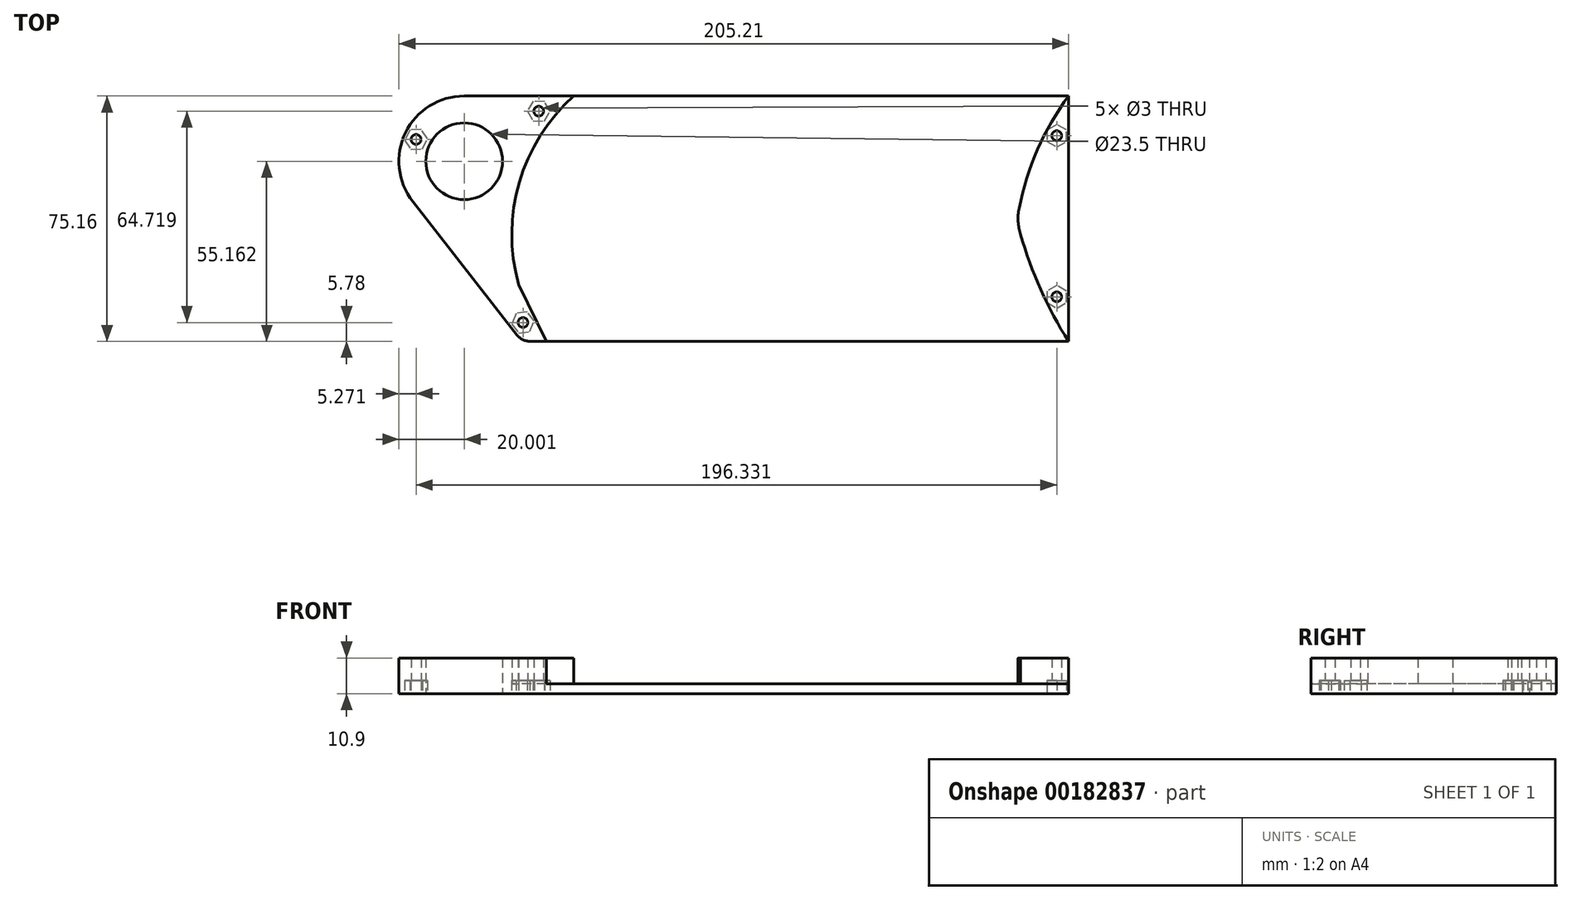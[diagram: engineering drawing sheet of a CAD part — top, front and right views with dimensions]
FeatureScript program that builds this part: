
annotation { "Feature Type Name" : "Feature", "Feature Type Description" : "" }
export const myFeature = defineFeature(function(context is Context, id is Id, definition is map)
    precondition{}
    {
        {
            var Q0;
            Q0=qCreatedBy(makeId("Top.planeOp"),FACE);
            var sketch = newSketch(context, id + "F0", { "sketchPlane" : qUnion([Q0])});
            skLineSegment(sketch, "E0", {"start": v(86, 37.87) * mm, "end": v(-99.2, 37.87) * mm});
            skLineSegment(sketch, "E1", {"start": v(86, -37.29) * mm, "end": v(-81.47, -37.29) * mm});
            skLineSegment(sketch, "E2.0", {"start": v(86, -37.29) * mm, "end": v(86, 37.87) * mm});
            skArc(sketch, "E3", {"start": v(70.84, 3.43) * mm, "mid": v(70.55, -0.57) * mm, "end": v(71.29, -4.5) * mm});
            skLineSegment(sketch, "E4", {"start": v(-73.97, -37.29) * mm, "end": v(-82.52, -19.87) * mm});
            skArc(sketch, "E5", {"start": v(-65.62, 37.87) * mm, "mid": v(-82.32, 11.42) * mm, "end": v(-82.52, -19.87) * mm});
            skArc(sketch, "E6", {"start": v(71.29, -4.5) * mm, "mid": v(77.46, -21.43) * mm, "end": v(86, -37.29) * mm});
            skCircle(sketch, "E7", {"center": v(-99.2, 17.87) * mm, "radius": 11.75 * mm});
            skLineSegment(sketch, "E8", {"start": v(-81.47, -37.29) * mm, "end": v(-114.97, 5.55) * mm});
            skArc(sketch, "E9", {"start": v(-99.2, 37.87) * mm, "mid": v(-117.19, 26.64) * mm, "end": v(-114.97, 5.55) * mm});
            skLineSegment(sketch, "E10", {"start": v(-73.97, -37.29) * mm, "end": v(-73.97, -48.25) * mm});
            skArc(sketch, "E11", {"start": v(86, 37.87) * mm, "mid": v(76.52, 21.49) * mm, "end": v(70.84, 3.43) * mm});
            skSolve(sketch);
        }
        {
            var Q0;
            Q0=makeQuery(id+"F0.imprint","IMPRINT",FACE,{"disambiguationData":[TD([[makeQuery(id+"F0.imprint","IMPRINT",EDGE,{"derivedFrom":sQuery(id+"F0.wireOp",EDGE,"E3")}),-1.0]])]});
            var sketch = newSketch(context, id + "F1", { "sketchPlane" : qUnion([Q0])});
            skSolve(sketch);
        }
        {
            var Q0;
            Q0 = qSketchRegion(id + "F1", true);
            var Q1;
            Q1=makeQuery(id+"F0.imprint","IMPRINT",FACE,{"disambiguationData":[TD([[makeQuery(id+"F0.imprint","IMPRINT",EDGE,{"derivedFrom":sQuery(id+"F0.wireOp",EDGE,"E3")}),-1.0]])]});
            extrude(context, id + "F2", {"entities" : qUnion([Q0, Q1]), "oppositeDirection" : true, "depth" : 3 * mm});
        }
        {
            var Q0;
            {var subQ3=sQuery(id+"F0.wireOp",EDGE,"E4");Q0=makeQuery(id+"F0.imprint","IMPRINT",FACE,{"disambiguationData":[TD([[makeQuery(id+"F0.imprint","IMPRINT",EDGE,{"derivedFrom":subQ3}),1.0]])]});}
            extrude(context, id + "F3", {"entities" : qUnion([Q0]), "depth" : 7.9 * mm});
        }
        {
            var Q0;
            {var subQ0=sQuery(id+"F0.wireOp",EDGE,"E2.0");Q0=makeQuery(id+"F0.imprint","IMPRINT",FACE,{"disambiguationData":[TD([[makeQuery(id+"F0.imprint","IMPRINT",EDGE,{"derivedFrom":subQ0}),1.0]])]});}
            extrude(context, id + "F4", {"entities" : qUnion([Q0]), "depth" : 7.9 * mm});
        }
        {
            var Q0;
            Q0=makeQuery(id+"F3.opExtrude","CAP_FACE",FACE,{"disambiguationData":[OSD([sQuery(id+"F0.wireOp",EDGE,"E0"),sQuery(id+"F0.wireOp",EDGE,"E1"),sQuery(id+"F0.wireOp",EDGE,"E4"),sQuery(id+"F0.wireOp",EDGE,"E5"),sQuery(id+"F0.wireOp",EDGE,"E7"),sQuery(id+"F0.wireOp",EDGE,"E8"),sQuery(id+"F0.wireOp",EDGE,"E9")])],"isStart":true});
            var Q1;
            Q1=makeQuery(id+"F4.opExtrude","CAP_FACE",FACE,{"disambiguationData":[OSD([sQuery(id+"F0.wireOp",EDGE,"E0"),sQuery(id+"F0.wireOp",EDGE,"E1"),sQuery(id+"F0.wireOp",EDGE,"E2.0"),sQuery(id+"F0.wireOp",EDGE,"E3"),sQuery(id+"F0.wireOp",EDGE,"uJdoGhJC-Amh7-iMku-Pf1O-IdhWUITwSaAr"),sQuery(id+"F0.wireOp",EDGE,"E6")])],"isStart":true});
            extrude(context, id + "F5", {"entities" : qUnion([Q0, Q1]), "depth" : 3 * mm});
        }
        {
            var Q0;
            Q0=makeQuery(id+"F3.opExtrude","SWEPT_EDGE",EDGE,{"disambiguationData":[OSD([sQuery(id+"F0.wireOp",EDGE,"E1"),sQuery(id+"F0.wireOp",EDGE,"E8")])]});
            var Q1;
            Q1=makeQuery(id+"F5.opExtrude","SWEPT_EDGE",EDGE,{"disambiguationData":[OSD([sQuery(id+"F0.wireOp",EDGE,"E1"),sQuery(id+"F0.wireOp",EDGE,"E8")])]});
            fillet(context, id + "F6", {"entities" : qUnion([Q0, Q1]), "radius" : 5 * mm, "tangentPropagation" : true, "allowEdgeOverflow" : false});
        }
        {
            var Q0;
            Q0=makeQuery(id+"F2.opExtrude","SWEPT_BODY",BODY,{"disambiguationData":[OSD([sQuery(id+"F0.wireOp",EDGE,"E0"),sQuery(id+"F0.wireOp",EDGE,"E1"),sQuery(id+"F0.wireOp",EDGE,"E3"),sQuery(id+"F0.wireOp",EDGE,"E4"),sQuery(id+"F0.wireOp",EDGE,"E5"),sQuery(id+"F0.wireOp",EDGE,"E6"),sQuery(id+"F0.wireOp",EDGE,"E11")])]});
            var Q1;
            Q1=makeQuery(id+"F3.opExtrude","SWEPT_BODY",BODY,{"disambiguationData":[OSD([sQuery(id+"F0.wireOp",EDGE,"E0"),sQuery(id+"F0.wireOp",EDGE,"E1"),sQuery(id+"F0.wireOp",EDGE,"E4"),sQuery(id+"F0.wireOp",EDGE,"E5"),sQuery(id+"F0.wireOp",EDGE,"E7"),sQuery(id+"F0.wireOp",EDGE,"E8"),sQuery(id+"F0.wireOp",EDGE,"E9")])]});
            var Q2;
            Q2=makeQuery(id+"F4.opExtrude","SWEPT_BODY",BODY,{"disambiguationData":[OSD([sQuery(id+"F0.wireOp",EDGE,"E2.0"),sQuery(id+"F0.wireOp",EDGE,"E3"),sQuery(id+"F0.wireOp",EDGE,"E6"),sQuery(id+"F0.wireOp",EDGE,"E11")])]});
            var Q3;
            Q3=makeQuery(id+"F5.opExtrude","SWEPT_BODY",BODY,{"disambiguationData":[OSD([sQuery(id+"F0.wireOp",EDGE,"E0"),sQuery(id+"F0.wireOp",EDGE,"E1"),sQuery(id+"F0.wireOp",EDGE,"E4"),sQuery(id+"F0.wireOp",EDGE,"E5"),sQuery(id+"F0.wireOp",EDGE,"E7"),sQuery(id+"F0.wireOp",EDGE,"E8"),sQuery(id+"F0.wireOp",EDGE,"E9")])]});
            var Q4;
            Q4=makeQuery(id+"F5.opExtrude","SWEPT_BODY",BODY,{"disambiguationData":[OSD([sQuery(id+"F0.wireOp",EDGE,"E2.0"),sQuery(id+"F0.wireOp",EDGE,"E3"),sQuery(id+"F0.wireOp",EDGE,"E6"),sQuery(id+"F0.wireOp",EDGE,"E11")])]});
            booleanBodies(context, id + "F7", {"operationType" : BooleanOperationType.UNION, "tools" : qUnion([Q0, Q1, Q2, Q3, Q4])});
        }
        {
            var Q0;
            {var subQ0=sQuery(id+"F0.wireOp",EDGE,"E5");var subQ1=sQuery(id+"F0.wireOp",EDGE,"E4");var subQ2=sQuery(id+"F0.wireOp",EDGE,"E1");var subQ3=sQuery(id+"F0.wireOp",EDGE,"E0");var subQ4=sQuery(id+"F0.wireOp",EDGE,"E11");var subQ5=sQuery(id+"F0.wireOp",EDGE,"E6");var subQ6=sQuery(id+"F0.wireOp",EDGE,"E3");Q0=makeQuery(id+"F7.opBoolean","MERGE",FACE,{"derivedFrom":[makeQuery(id+"F2.opExtrude","CAP_FACE",FACE,{"disambiguationData":[OSD([subQ3,subQ2,subQ6,subQ1,subQ0,subQ5,subQ4])],"isStart":false}),makeQuery(id+"F5.opExtrude","CAP_FACE",FACE,{"disambiguationData":[OSD([sQuery(id+"F0.wireOp",EDGE,"E2.0"),subQ6,subQ5,subQ4])],"isStart":false}),makeQuery(id+"F5.opExtrude","CAP_FACE",FACE,{"disambiguationData":[OSD([subQ3,subQ2,subQ1,subQ0,sQuery(id+"F0.wireOp",EDGE,"E7"),sQuery(id+"F0.wireOp",EDGE,"E8"),sQuery(id+"F0.wireOp",EDGE,"E9")])],"isStart":false})]});}
            var sketch = newSketch(context, id + "F8", { "sketchPlane" : qUnion([Q0])});
            skPoint(sketch, "E12", {"position": v(-81.19, 31.5) * mm});
            skPoint(sketch, "E13", {"position": v(-76.36, -33.2) * mm});
            skPoint(sketch, "E14", {"position": v(-113.94, -24.55) * mm});
            skCircle(sketch, "E15.cCircle", {"center": v(-76.36, -33.2) * mm, "radius": 3 * mm, "construction": true});
            skLineSegment(sketch, "E15.0", {"start": v(-72.9, -33.15) * mm, "end": v(-74.57, -36.18) * mm});
            skLineSegment(sketch, "E15.1", {"start": v(-74.57, -36.18) * mm, "end": v(-78.04, -36.24) * mm});
            skLineSegment(sketch, "E15.2", {"start": v(-78.04, -36.24) * mm, "end": v(-79.82, -33.27) * mm});
            skLineSegment(sketch, "E15.3", {"start": v(-79.82, -33.27) * mm, "end": v(-78.14, -30.24) * mm});
            skLineSegment(sketch, "E15.4", {"start": v(-78.14, -30.24) * mm, "end": v(-74.67, -30.18) * mm});
            skLineSegment(sketch, "E15.5", {"start": v(-74.67, -30.18) * mm, "end": v(-72.9, -33.15) * mm});
            skPoint(sketch, "E15.0.midPoint", {"position": v(-73.73, -34.67) * mm});
            skPoint(sketch, "E16", {"position": v(82.4, 23.66) * mm});
            skPoint(sketch, "E17", {"position": v(82.4, -25.7) * mm});
            skCircle(sketch, "E18.cCircle", {"center": v(82.4, 23.66) * mm, "radius": 3 * mm, "construction": true});
            skLineSegment(sketch, "E18.0", {"start": v(85.4, 25.4) * mm, "end": v(85.4, 21.93) * mm});
            skLineSegment(sketch, "E18.1", {"start": v(85.4, 21.93) * mm, "end": v(82.4, 20.2) * mm});
            skLineSegment(sketch, "E18.2", {"start": v(82.4, 20.2) * mm, "end": v(79.4, 21.93) * mm});
            skLineSegment(sketch, "E18.3", {"start": v(79.4, 21.93) * mm, "end": v(79.4, 25.4) * mm});
            skLineSegment(sketch, "E18.4", {"start": v(79.4, 25.4) * mm, "end": v(82.4, 27.13) * mm});
            skLineSegment(sketch, "E18.5", {"start": v(82.4, 27.13) * mm, "end": v(85.4, 25.4) * mm});
            skPoint(sketch, "E18.0.midPoint", {"position": v(85.4, 23.66) * mm});
            skCircle(sketch, "E19.cCircle", {"center": v(82.4, -25.7) * mm, "radius": 3 * mm, "construction": true});
            skLineSegment(sketch, "E19.0", {"start": v(85.4, -23.97) * mm, "end": v(85.4, -27.43) * mm});
            skLineSegment(sketch, "E19.1", {"start": v(85.4, -27.43) * mm, "end": v(82.4, -29.16) * mm});
            skLineSegment(sketch, "E19.2", {"start": v(82.4, -29.16) * mm, "end": v(79.4, -27.43) * mm});
            skLineSegment(sketch, "E19.3", {"start": v(79.4, -27.43) * mm, "end": v(79.4, -23.97) * mm});
            skLineSegment(sketch, "E19.4", {"start": v(79.4, -23.97) * mm, "end": v(82.4, -22.24) * mm});
            skLineSegment(sketch, "E19.5", {"start": v(82.4, -22.24) * mm, "end": v(85.4, -23.97) * mm});
            skPoint(sketch, "E19.0.midPoint", {"position": v(85.4, -25.7) * mm});
            skCircle(sketch, "E20.cCircle", {"center": v(-81.19, 31.5) * mm, "radius": 3 * mm, "construction": true});
            skLineSegment(sketch, "E20.0", {"start": v(-77.76, 31.04) * mm, "end": v(-79.88, 28.3) * mm});
            skLineSegment(sketch, "E20.1", {"start": v(-79.88, 28.3) * mm, "end": v(-83.3, 28.77) * mm});
            skLineSegment(sketch, "E20.2", {"start": v(-83.3, 28.77) * mm, "end": v(-84.62, 31.98) * mm});
            skLineSegment(sketch, "E20.3", {"start": v(-84.62, 31.98) * mm, "end": v(-82.5, 34.72) * mm});
            skLineSegment(sketch, "E20.4", {"start": v(-82.5, 34.72) * mm, "end": v(-79.07, 34.25) * mm});
            skLineSegment(sketch, "E20.5", {"start": v(-79.07, 34.25) * mm, "end": v(-77.76, 31.04) * mm});
            skPoint(sketch, "E20.0.midPoint", {"position": v(-78.82, 29.67) * mm});
            skCircle(sketch, "E21.cCircle", {"center": v(-113.94, -24.55) * mm, "radius": 3 * mm, "construction": true});
            skLineSegment(sketch, "E21.0", {"start": v(-112.04, -21.66) * mm, "end": v(-110.48, -24.76) * mm});
            skLineSegment(sketch, "E21.1", {"start": v(-110.48, -24.76) * mm, "end": v(-112.38, -27.65) * mm});
            skLineSegment(sketch, "E21.2", {"start": v(-112.38, -27.65) * mm, "end": v(-115.84, -27.45) * mm});
            skLineSegment(sketch, "E21.3", {"start": v(-115.84, -27.45) * mm, "end": v(-117.4, -24.35) * mm});
            skLineSegment(sketch, "E21.4", {"start": v(-117.4, -24.35) * mm, "end": v(-115.5, -21.46) * mm});
            skLineSegment(sketch, "E21.5", {"start": v(-115.5, -21.46) * mm, "end": v(-112.04, -21.66) * mm});
            skPoint(sketch, "E21.0.midPoint", {"position": v(-111.26, -23.2) * mm});
            skSolve(sketch);
        }
        {
            var Q0;
            Q0=sQuery(id+"F8.wireOp",VERTEX,"E12");
            var Q1;
            Q1=sQuery(id+"F8.wireOp",VERTEX,"E14");
            var Q2;
            Q2=sQuery(id+"F8.wireOp",VERTEX,"E13");
            var Q3;
            Q3=sQuery(id+"F8.wireOp",VERTEX,"E16");
            var Q4;
            Q4=sQuery(id+"F8.wireOp",VERTEX,"E17");
            var Q5;
            Q5=makeQuery(id+"F2.opExtrude","SWEPT_BODY",BODY,{"disambiguationData":[OSD([sQuery(id+"F0.wireOp",EDGE,"E0"),sQuery(id+"F0.wireOp",EDGE,"E1"),sQuery(id+"F0.wireOp",EDGE,"E3"),sQuery(id+"F0.wireOp",EDGE,"E4"),sQuery(id+"F0.wireOp",EDGE,"E5"),sQuery(id+"F0.wireOp",EDGE,"E6"),sQuery(id+"F0.wireOp",EDGE,"E11")])]});
            hole(context, id + "F9", {"style" : HoleStyle.SIMPLE, "endStyle" : HoleEndStyle.THROUGH, "holeDiameter" : 3 * mm, "startFromSketch" : true, "locations" : qUnion([Q0, Q1, Q2, Q3, Q4]), "scope" : qUnion([Q5]), "isTappedThrough" : true});
        }
        {
            var Q0;
            Q0 = qSketchRegion(id + "F8", true);
            extrude(context, id + "F10", {"entities" : qUnion([Q0]), "operationType" : NewBodyOperationType.REMOVE, "oppositeDirection" : true, "depth" : 4 * mm});
        }
        {
            var Q0;
            Q0 = qSketchRegion(id + "F8", true);
            extrude(context, id + "F11", {"entities" : qUnion([Q0]), "operationType" : NewBodyOperationType.REMOVE, "oppositeDirection" : true, "depth" : 4 * mm});
        }
    });
